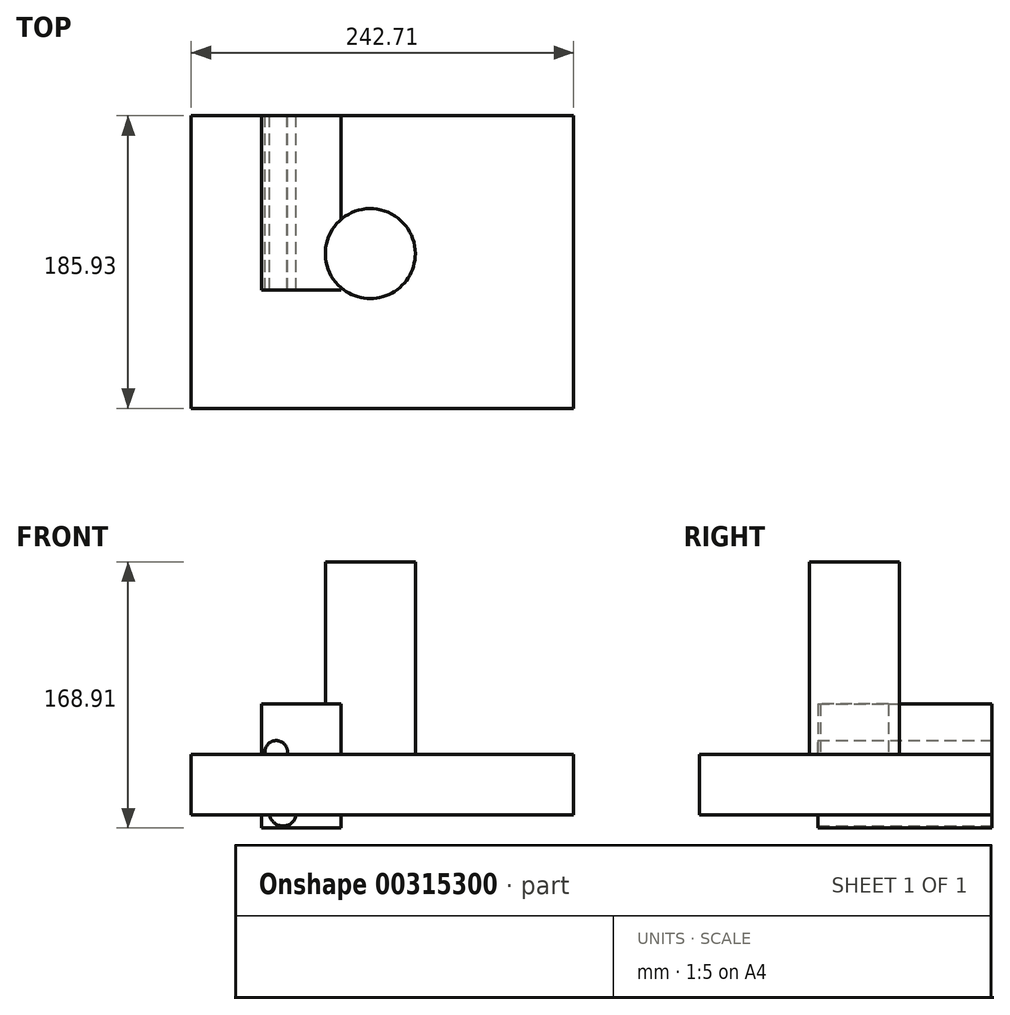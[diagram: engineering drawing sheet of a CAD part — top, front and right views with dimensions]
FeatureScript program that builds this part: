
annotation { "Feature Type Name" : "Feature", "Feature Type Description" : "" }
export const myFeature = defineFeature(function(context is Context, id is Id, definition is map)
    precondition{}
    {
        {
            var Q0;
            Q0=qCreatedBy(makeId("Front.planeOp"),FACE);
            var sketch = newSketch(context, id + "F0", { "sketchPlane" : qUnion([Q0])});
            skLineSegment(sketch, "E0.bottom", {"start": v(-126.26, -31.85) * mm, "end": v(116.45, -31.85) * mm});
            skLineSegment(sketch, "E0.top", {"start": v(-126.26, -70.27) * mm, "end": v(116.45, -70.27) * mm});
            skLineSegment(sketch, "E0.left", {"start": v(-126.26, -31.85) * mm, "end": v(-126.26, -70.27) * mm});
            skLineSegment(sketch, "E0.right", {"start": v(116.45, -31.85) * mm, "end": v(116.45, -70.27) * mm});
            skSolve(sketch);
        }
        {
            var Q0;
            Q0 = qSketchRegion(id + "F0", true);
            extrude(context, id + "F1", {"entities" : qUnion([Q0]), "depth" : 185.93 * mm});
        }
        {
            var Q0;
            Q0=makeQuery(id+"F1.opExtrude","SWEPT_FACE",FACE,{"disambiguationData":[OSD([sQuery(id+"F0.wireOp",EDGE,"E0.bottom")])]});
            var sketch = newSketch(context, id + "F2", { "sketchPlane" : qUnion([Q0])});
            skCircle(sketch, "E1", {"center": v(-12.56, -87.58) * mm, "radius": 28.57 * mm});
            skSolve(sketch);
        }
        {
            var Q0;
            Q0 = qSketchRegion(id + "F2", true);
            extrude(context, id + "F3", {"entities" : qUnion([Q0]), "operationType" : NewBodyOperationType.ADD, "depth" : 122.17 * mm});
        }
        {
            var Q0;
            Q0=qCreatedBy(makeId("Front.planeOp"),FACE);
            var sketch = newSketch(context, id + "F4", { "sketchPlane" : qUnion([Q0])});
            skLineSegment(sketch, "E2.bottom", {"start": v(-81.52, 0) * mm, "end": v(-31.26, 0) * mm});
            skLineSegment(sketch, "E2.top", {"start": v(-81.52, -78.6) * mm, "end": v(-31.26, -78.6) * mm});
            skLineSegment(sketch, "E2.left", {"start": v(-81.52, 0) * mm, "end": v(-81.52, -78.6) * mm});
            skLineSegment(sketch, "E2.right", {"start": v(-31.26, 0) * mm, "end": v(-31.26, -78.6) * mm});
            skCircle(sketch, "E3", {"center": v(-72.32, -30.38) * mm, "radius": 7.18 * mm});
            skCircle(sketch, "E4", {"center": v(-47.2, -37.22) * mm, "radius": 5.02 * mm});
            skCircle(sketch, "E5", {"center": v(-68.03, -68.98) * mm, "radius": 8.53 * mm});
            skCircle(sketch, "E6", {"center": v(-42.3, -64) * mm, "radius": 11.82 * mm});
            skSolve(sketch);
        }
        {
            var Q0;
            Q0 = qSketchRegion(id + "F4", true);
            extrude(context, id + "F5", {"entities" : qUnion([Q0]), "operationType" : NewBodyOperationType.ADD, "depth" : 110.74 * mm});
        }
    });
